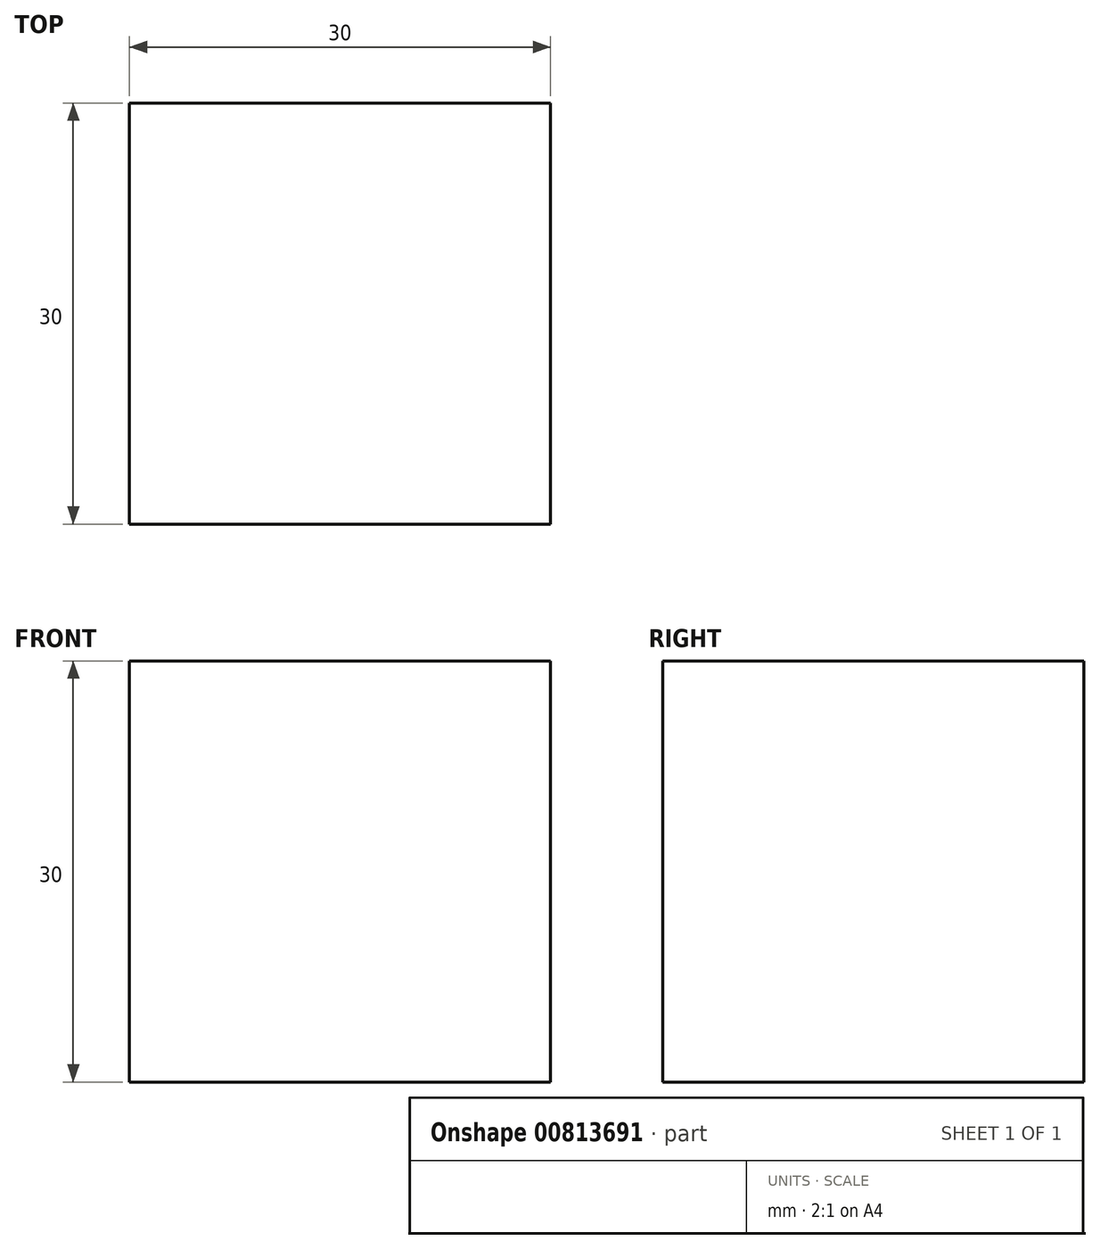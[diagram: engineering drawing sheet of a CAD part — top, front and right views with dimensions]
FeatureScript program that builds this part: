
annotation { "Feature Type Name" : "Feature", "Feature Type Description" : "" }
export const myFeature = defineFeature(function(context is Context, id is Id, definition is map)
    precondition{}
    {
        {
            var Q0;
            Q0=qCreatedBy(makeId("Front.planeOp"),FACE);
            var sketch = newSketch(context, id + "F0", { "sketchPlane" : qUnion([Q0])});
            skLineSegment(sketch, "E0.bottom", {"start": v(15, 15) * mm, "end": v(-15, 15) * mm});
            skLineSegment(sketch, "E0.top", {"start": v(15, -15) * mm, "end": v(-15, -15) * mm});
            skLineSegment(sketch, "E0.left", {"start": v(15, 15) * mm, "end": v(15, -15) * mm});
            skLineSegment(sketch, "E0.right", {"start": v(-15, 15) * mm, "end": v(-15, -15) * mm});
            skPoint(sketch, "E0.middle", {"position": v(0, 0) * mm});
            skSolve(sketch);
        }
        {
            var Q0;
            Q0 = qSketchRegion(id + "F0", true);
            extrude(context, id + "F1", {"entities" : qUnion([Q0]), "endBound" : BoundingType.SYMMETRIC, "depth" : 30 * mm, "offsetDistance" : 25 * mm});
        }
    });
